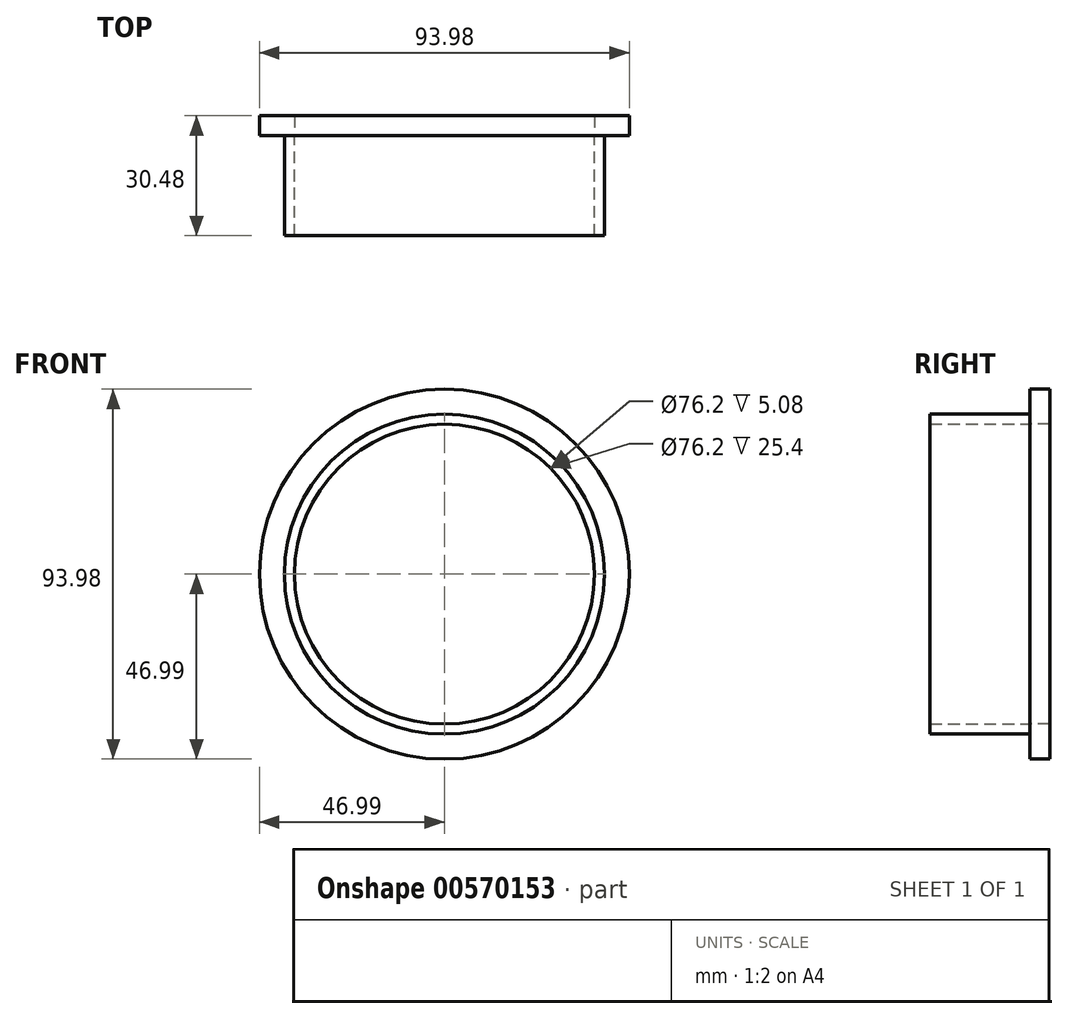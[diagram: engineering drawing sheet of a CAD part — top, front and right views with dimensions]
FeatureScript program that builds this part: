
annotation { "Feature Type Name" : "Feature", "Feature Type Description" : "" }
export const myFeature = defineFeature(function(context is Context, id is Id, definition is map)
    precondition{}
    {
        {
            var Q0;
            Q0=qCreatedBy(makeId("Front.planeOp"),FACE);
            var sketch = newSketch(context, id + "F0", { "sketchPlane" : qUnion([Q0])});
            skCircle(sketch, "E0", {"center": v(0, 0) * mm, "radius": 38.1 * mm});
            skCircle(sketch, "E1", {"center": v(0, 0) * mm, "radius": 40.64 * mm});
            skCircle(sketch, "E2", {"center": v(0, 0) * mm, "radius": 47 * mm});
            skSolve(sketch);
        }
        {
            var Q0;
            Q0=makeQuery(id+"F0.imprint","IMPRINT",FACE,{"disambiguationData":[TD([[makeQuery(id+"F0.imprint","IMPRINT",EDGE,{"derivedFrom":sQuery(id+"F0.wireOp",EDGE,"E0")}),-1.0]])]});
            extrude(context, id + "F1", {"entities" : qUnion([Q0]), "depth" : 25.4 * mm, "offsetDistance" : 25.4 * mm});
        }
        {
            var Q0;
            Q0=makeQuery(id+"F0.imprint","IMPRINT",FACE,{"disambiguationData":[TD([[makeQuery(id+"F0.imprint","IMPRINT",EDGE,{"derivedFrom":sQuery(id+"F0.wireOp",EDGE,"E1")}),-1.0]])]});
            var Q1;
            Q1=makeQuery(id+"F0.imprint","IMPRINT",FACE,{"disambiguationData":[TD([[makeQuery(id+"F0.imprint","IMPRINT",EDGE,{"derivedFrom":sQuery(id+"F0.wireOp",EDGE,"E0")}),-1.0]])]});
            extrude(context, id + "F2", {"entities" : qUnion([Q0, Q1]), "oppositeDirection" : true, "depth" : 5.08 * mm, "offsetDistance" : 25.4 * mm});
        }
    });
